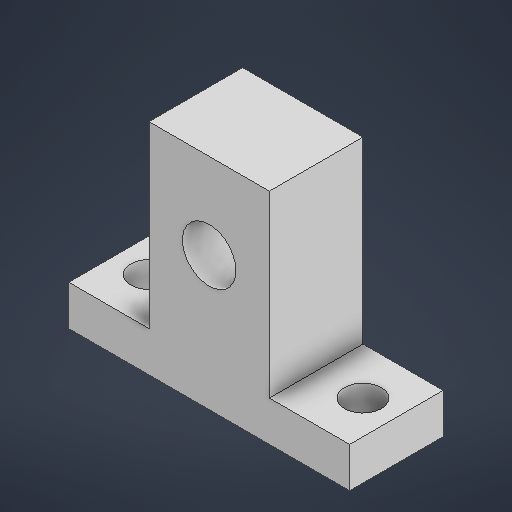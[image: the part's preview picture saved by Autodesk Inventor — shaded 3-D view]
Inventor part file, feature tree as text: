
AUTODESK INVENTOR PART (.ipt)
format: ipt  version: 2025.1 (Build 291241000, 241)  size: 205,824 bytes
history: native  units: mm
features: extrude x2, sketch x2, projected_geometry x2
ambient origin geometry x8: Origin, YZ Plane, XZ Plane, XY Plane, X Axis, Y Axis, Z Axis, Center Point
bodies: Solid1 (feature_tree)
feature tree (6):
  extrude  "Extrusion1"  Depth=18.0mm
  extrude  "Extrusion2"  Depth=6.0mm
  sketch  "Sketch1"  dims[d2=8.0mm d3=18.0mm]
  sketch  "Sketch2"  dims[d4=20.0mm d5=6.0mm d6=32.8mm d7=42.0mm d8=14.0mm d9=0.0mm d10=5.5mm d11=16.0mm d12=5.5mm d13=16.0mm d14=0.0mm d15=0.0mm]
  projected_geometry  "Projected Loop1"
  projected_geometry  "Projected Loop2"
